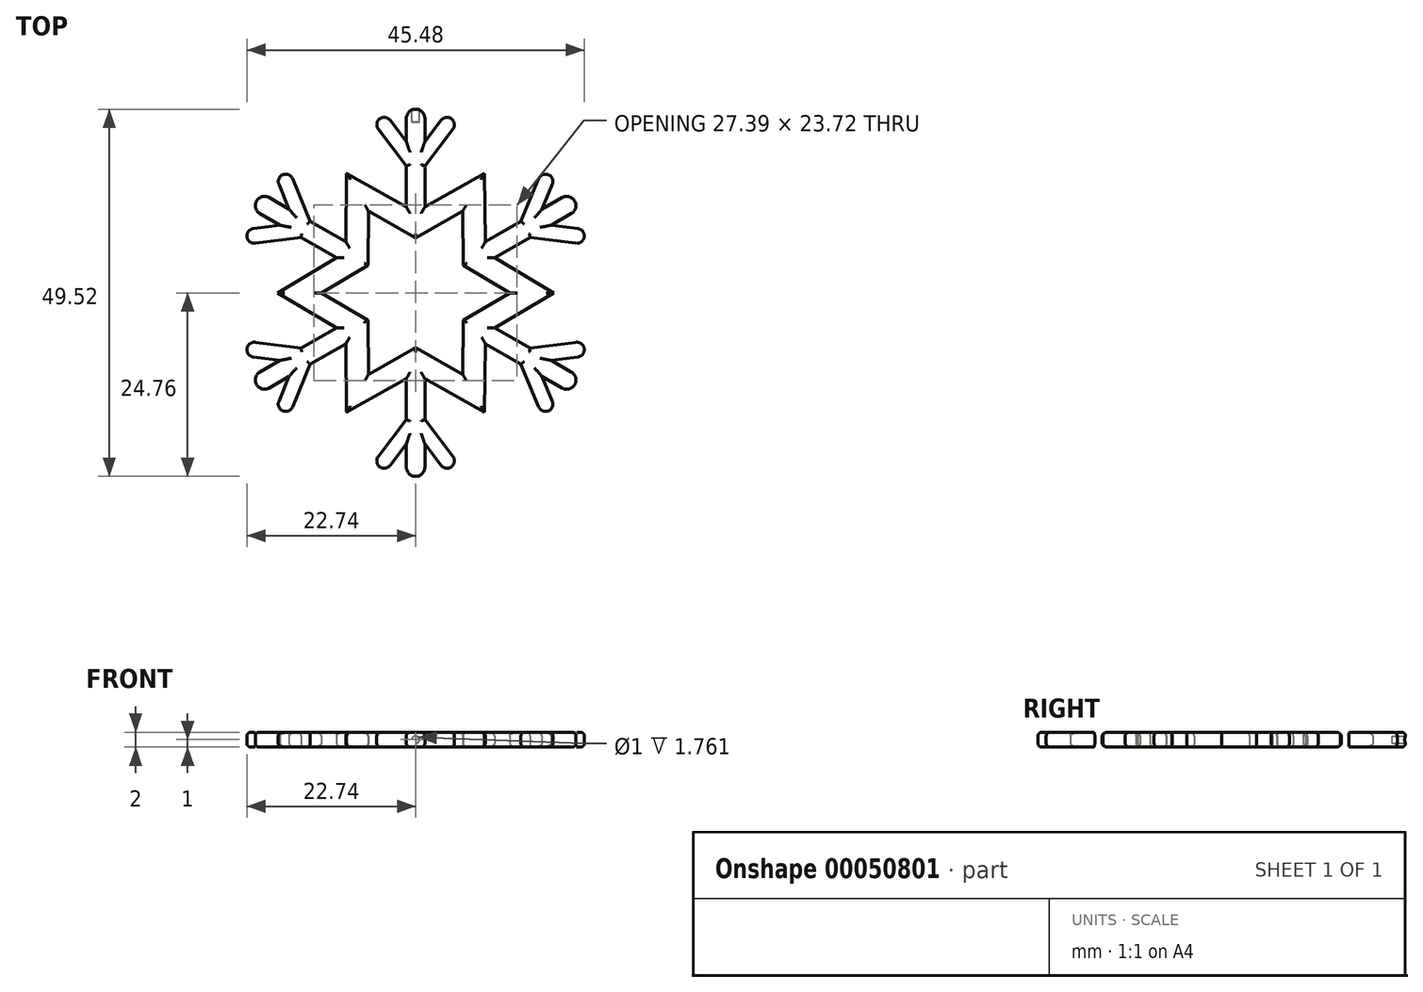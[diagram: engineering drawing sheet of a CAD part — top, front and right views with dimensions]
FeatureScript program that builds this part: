
annotation { "Feature Type Name" : "Feature", "Feature Type Description" : "" }
export const myFeature = defineFeature(function(context is Context, id is Id, definition is map)
    precondition{}
    {
        {
            var Q0;
            Q0=qCreatedBy(makeId("Top.planeOp"),FACE);
            var sketch = newSketch(context, id + "F0", { "sketchPlane" : qUnion([Q0])});
            skCircle(sketch, "E0", {"center": v(0, 0) * mm, "radius": 25 * mm, "construction": true});
            skLineSegment(sketch, "E1", {"start": v(0, 0) * mm, "end": v(0, 37.67) * mm, "construction": true});
            skLineSegment(sketch, "E2", {"start": v(0, 0) * mm, "end": v(15.8, 27.37) * mm, "construction": true});
            skLineSegment(sketch, "E3", {"start": v(0, 0) * mm, "end": v(-17.9, 31.01) * mm, "construction": true});
            skLineSegment(sketch, "E4", {"start": v(1.25, 23.51) * mm, "end": v(1.25, 20.4) * mm});
            skLineSegment(sketch, "E5", {"start": v(1.25, 20.4) * mm, "end": v(3.44, 23.27) * mm});
            skLineSegment(sketch, "E6", {"start": v(5.03, 22.05) * mm, "end": v(1.25, 17.11) * mm});
            skLineSegment(sketch, "E7", {"start": v(1.25, 17.11) * mm, "end": v(1.25, 11.57) * mm});
            skLineSegment(sketch, "E8", {"start": v(1.25, 11.57) * mm, "end": v(9.3, 16.11) * mm});
            skLineSegment(sketch, "E9", {"start": v(9.3, 16.11) * mm, "end": v(6.36, 11) * mm});
            skLineSegment(sketch, "E10", {"start": v(6.36, 11) * mm, "end": v(0, 7.43) * mm});
            skLineSegment(sketch, "E11.MirrorCS", {"start": v(-6.36, 11) * mm, "end": v(0, 7.43) * mm});
            skLineSegment(sketch, "E12.MirrorCS", {"start": v(-1.25, 17.11) * mm, "end": v(-1.25, 11.57) * mm});
            skLineSegment(sketch, "E13.MirrorCS", {"start": v(-1.25, 11.57) * mm, "end": v(-9.3, 16.11) * mm});
            skLineSegment(sketch, "E14.MirrorCS", {"start": v(-1.25, 20.4) * mm, "end": v(-3.44, 23.27) * mm});
            skLineSegment(sketch, "E15.MirrorCS", {"start": v(-9.3, 16.11) * mm, "end": v(-6.36, 11) * mm});
            skLineSegment(sketch, "E16.MirrorCS", {"start": v(-1.25, 23.51) * mm, "end": v(-1.25, 20.4) * mm});
            skLineSegment(sketch, "E17.MirrorCS", {"start": v(-5.03, 22.05) * mm, "end": v(-1.25, 17.11) * mm});
            skArc(sketch, "E18", {"start": v(-1.25, 23.51) * mm, "mid": v(0, 24.76) * mm, "end": v(1.25, 23.51) * mm});
            skArc(sketch, "E19", {"start": v(3.44, 23.27) * mm, "mid": v(4.84, 23.45) * mm, "end": v(5.03, 22.05) * mm});
            skArc(sketch, "E20", {"start": v(-3.44, 23.27) * mm, "mid": v(-4.84, 23.45) * mm, "end": v(-5.03, 22.05) * mm});
            skSolve(sketch);
        }
        {
            var Q0;
            Q0=makeQuery(id+"F0.imprint","IMPRINT",FACE,{"disambiguationData":[TD([[makeQuery(id+"F0.imprint","IMPRINT",EDGE,{"derivedFrom":sQuery(id+"F0.wireOp",EDGE,"E4")}),-1.0]])]});
            extrude(context, id + "F1", {"entities" : qUnion([Q0]), "endBound" : BoundingType.SYMMETRIC, "depth" : 2 * mm});
        }
        {
            var Q0;
            Q0=qCreatedBy(makeId("Front.planeOp"),FACE);
            var sketch = newSketch(context, id + "F2", { "sketchPlane" : qUnion([Q0])});
            skLineSegment(sketch, "E21", {"start": v(0, -15.67) * mm, "end": v(0, 28.6) * mm, "construction": true});
            skSolve(sketch);
        }
        {
            var Q0;
            Q0=makeQuery(id+"F1.opExtrude","SWEPT_BODY",BODY,{"disambiguationData":[OSD([sQuery(id+"F0.wireOp",EDGE,"E4"),sQuery(id+"F0.wireOp",EDGE,"E5"),sQuery(id+"F0.wireOp",EDGE,"E6"),sQuery(id+"F0.wireOp",EDGE,"E7"),sQuery(id+"F0.wireOp",EDGE,"E8"),sQuery(id+"F0.wireOp",EDGE,"E9"),sQuery(id+"F0.wireOp",EDGE,"E10"),sQuery(id+"F0.wireOp",EDGE,"E11.MirrorCS"),sQuery(id+"F0.wireOp",EDGE,"E12.MirrorCS"),sQuery(id+"F0.wireOp",EDGE,"E13.MirrorCS"),sQuery(id+"F0.wireOp",EDGE,"E14.MirrorCS"),sQuery(id+"F0.wireOp",EDGE,"E15.MirrorCS"),sQuery(id+"F0.wireOp",EDGE,"E16.MirrorCS"),sQuery(id+"F0.wireOp",EDGE,"E17.MirrorCS"),sQuery(id+"F0.wireOp",EDGE,"E18"),sQuery(id+"F0.wireOp",EDGE,"E19"),sQuery(id+"F0.wireOp",EDGE,"E20")])]});
            var Q1;
            Q1=sQuery(id+"F2.wireOp",EDGE,"E21");
            circularPattern(context, id + "F3", {"operationType" : NewBodyOperationType.ADD, "entities" : qUnion([Q0]), "axis" : qUnion([Q1]), "angle" : 360 * degree, "instanceCount" : round(6), "equalSpace" : true});
        }
        {
            var Q0;
            {var subQ0=makeQuery(id+"F1.opExtrude","CAP_FACE",FACE,{"disambiguationData":[OSD([sQuery(id+"F0.wireOp",EDGE,"E4"),sQuery(id+"F0.wireOp",EDGE,"E5"),sQuery(id+"F0.wireOp",EDGE,"E6"),sQuery(id+"F0.wireOp",EDGE,"E7"),sQuery(id+"F0.wireOp",EDGE,"E8"),sQuery(id+"F0.wireOp",EDGE,"E9"),sQuery(id+"F0.wireOp",EDGE,"E10"),sQuery(id+"F0.wireOp",EDGE,"E11.MirrorCS"),sQuery(id+"F0.wireOp",EDGE,"E12.MirrorCS"),sQuery(id+"F0.wireOp",EDGE,"E13.MirrorCS"),sQuery(id+"F0.wireOp",EDGE,"E14.MirrorCS"),sQuery(id+"F0.wireOp",EDGE,"E15.MirrorCS"),sQuery(id+"F0.wireOp",EDGE,"E16.MirrorCS"),sQuery(id+"F0.wireOp",EDGE,"E17.MirrorCS"),sQuery(id+"F0.wireOp",EDGE,"E18"),sQuery(id+"F0.wireOp",EDGE,"E19"),sQuery(id+"F0.wireOp",EDGE,"E20")])],"isStart":false});Q0=makeQuery(id+"F3.boolean.opBoolean","MERGE",FACE,{"derivedFrom":[subQ0,makeQuery(id+"F3.opPattern","COPY",FACE,{"derivedFrom":subQ0,"instanceName":"1"}),makeQuery(id+"F3.opPattern","COPY",FACE,{"derivedFrom":subQ0,"instanceName":"2"}),makeQuery(id+"F3.opPattern","COPY",FACE,{"derivedFrom":subQ0,"instanceName":"3"}),makeQuery(id+"F3.opPattern","COPY",FACE,{"derivedFrom":subQ0,"instanceName":"4"}),makeQuery(id+"F3.opPattern","COPY",FACE,{"derivedFrom":subQ0,"instanceName":"5"})]});}
            var Q1;
            {var subQ0=makeQuery(id+"F1.opExtrude","CAP_FACE",FACE,{"disambiguationData":[OSD([sQuery(id+"F0.wireOp",EDGE,"E4"),sQuery(id+"F0.wireOp",EDGE,"E5"),sQuery(id+"F0.wireOp",EDGE,"E6"),sQuery(id+"F0.wireOp",EDGE,"E7"),sQuery(id+"F0.wireOp",EDGE,"E8"),sQuery(id+"F0.wireOp",EDGE,"E9"),sQuery(id+"F0.wireOp",EDGE,"E10"),sQuery(id+"F0.wireOp",EDGE,"E11.MirrorCS"),sQuery(id+"F0.wireOp",EDGE,"E12.MirrorCS"),sQuery(id+"F0.wireOp",EDGE,"E13.MirrorCS"),sQuery(id+"F0.wireOp",EDGE,"E14.MirrorCS"),sQuery(id+"F0.wireOp",EDGE,"E15.MirrorCS"),sQuery(id+"F0.wireOp",EDGE,"E16.MirrorCS"),sQuery(id+"F0.wireOp",EDGE,"E17.MirrorCS"),sQuery(id+"F0.wireOp",EDGE,"E18"),sQuery(id+"F0.wireOp",EDGE,"E19"),sQuery(id+"F0.wireOp",EDGE,"E20")])],"isStart":true});Q1=makeQuery(id+"F3.boolean.opBoolean","MERGE",FACE,{"derivedFrom":[subQ0,makeQuery(id+"F3.opPattern","COPY",FACE,{"derivedFrom":subQ0,"instanceName":"1"}),makeQuery(id+"F3.opPattern","COPY",FACE,{"derivedFrom":subQ0,"instanceName":"2"}),makeQuery(id+"F3.opPattern","COPY",FACE,{"derivedFrom":subQ0,"instanceName":"3"}),makeQuery(id+"F3.opPattern","COPY",FACE,{"derivedFrom":subQ0,"instanceName":"4"}),makeQuery(id+"F3.opPattern","COPY",FACE,{"derivedFrom":subQ0,"instanceName":"5"})]});}
            fillet(context, id + "F4", {"entities" : qUnion([Q0, Q1]), "radius" : 0.5 * mm, "tangentPropagation" : true, "allowEdgeOverflow" : false});
        }
        {
            var Q0;
            Q0=qCreatedBy(makeId("Front.planeOp"),FACE);
            cPlane(context, id + "F5", {"entities" : qUnion([Q0]), "cplaneType" : CPlaneType.OFFSET, "offset" : 25 * mm, "oppositeDirection" : true, "width" : 150 * mm, "height" : 150 * mm});
        }
        {
            var Q0;
            Q0=qCreatedBy(id+"F5.planeOp",FACE);
            var sketch = newSketch(context, id + "F6", { "sketchPlane" : qUnion([Q0])});
            skCircle(sketch, "E22", {"center": v(0, 0) * mm, "radius": 0.5 * mm});
            skSolve(sketch);
        }
        {
            var Q0;
            Q0=makeQuery(id+"F6.imprint","IMPRINT",FACE,{"disambiguationData":[TD([[makeQuery(id+"F6.imprint","IMPRINT",EDGE,{"derivedFrom":sQuery(id+"F6.wireOp",EDGE,"E22")}),1.0]])]});
            extrude(context, id + "F7", {"entities" : qUnion([Q0]), "operationType" : NewBodyOperationType.REMOVE, "depth" : 2 * mm});
        }
    });
